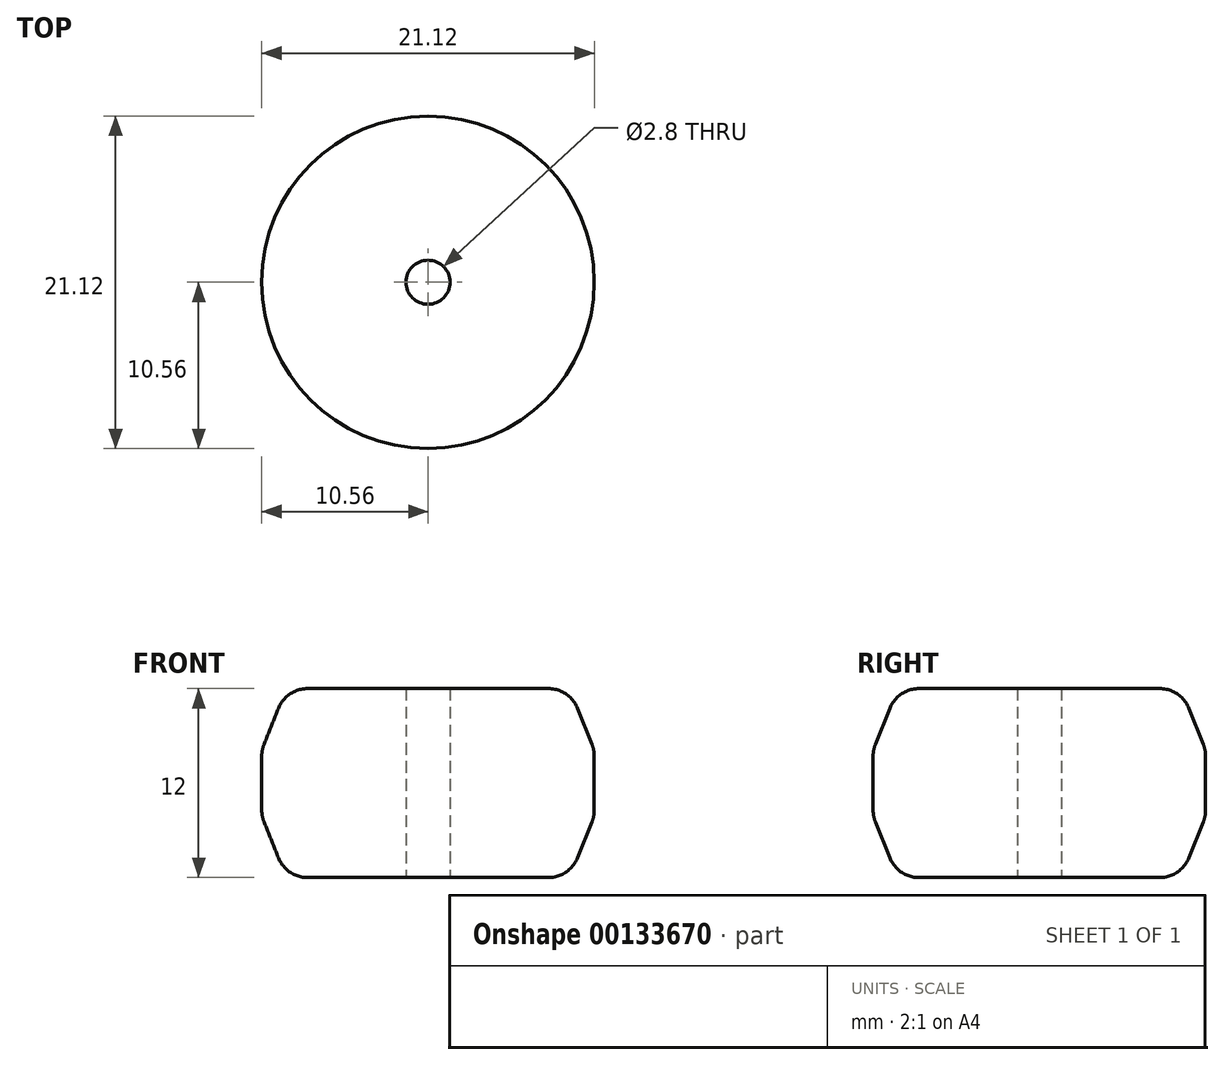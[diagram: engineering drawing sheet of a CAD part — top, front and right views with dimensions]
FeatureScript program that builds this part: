
annotation { "Feature Type Name" : "Feature", "Feature Type Description" : "" }
export const myFeature = defineFeature(function(context is Context, id is Id, definition is map)
    precondition{}
    {
        {
            var Q0;
            Q0=qCreatedBy(makeId("Top.planeOp"),FACE);
            var sketch = newSketch(context, id + "F0", { "sketchPlane" : qUnion([Q0])});
            skCircle(sketch, "E0", {"center": v(0, 0) * mm, "radius": 1.4 * mm});
            skCircle(sketch, "E1", {"center": v(0, 0) * mm, "radius": 9 * mm});
            skSolve(sketch);
        }
        {
            var Q0;
            Q0=makeQuery(id+"F0.imprint","IMPRINT",FACE,{"disambiguationData":[TD([[makeQuery(id+"F0.imprint","IMPRINT",EDGE,{"derivedFrom":sQuery(id+"F0.wireOp",EDGE,"E0")}),-1.0]])]});
            extrude(context, id + "F1", {"entities" : qUnion([Q0]), "depth" : 12 * mm});
        }
        {
            var Q0;
            Q0=qCreatedBy(makeId("Front.planeOp"),FACE);
            var sketch = newSketch(context, id + "F2", { "sketchPlane" : qUnion([Q0])});
            skLineSegment(sketch, "E2", {"start": v(-9, 0) * mm, "end": v(-9, 12) * mm});
            skLineSegment(sketch, "E3", {"start": v(-9, 0) * mm, "end": v(0, 0) * mm});
            skLineSegment(sketch, "E4", {"start": v(-9, 0) * mm, "end": v(-10.56, 3.9) * mm});
            skLineSegment(sketch, "E5", {"start": v(-10.56, 3.9) * mm, "end": v(-10.56, 8.1) * mm});
            skLineSegment(sketch, "E6", {"start": v(-10.56, 8.1) * mm, "end": v(-9, 12) * mm});
            skSolve(sketch);
        }
        {
            var Q0;
            Q0=qSketchRegion(id+"F2",true);
            var Q1;
            Q1=makeQuery(id+"F1.opExtrude","CAP_EDGE",EDGE,{"disambiguationData":[OSD([sQuery(id+"F0.wireOp",EDGE,"E1")])],"isStart":false});
            revolve(context, id + "F3", {"operationType" : NewBodyOperationType.ADD, "entities" : qUnion([Q0]), "axis" : qUnion([Q1]), "revolveType" : RevolveType.FULL, "oppositeDirection" : true});
        }
        {
            var Q0;
            Q0=makeQuery(id+"F3.opRevolve","SWEPT_EDGE",EDGE,{"disambiguationData":[OSD([sQuery(id+"F2.wireOp",EDGE,"E4"),sQuery(id+"F2.wireOp",EDGE,"E5")])]});
            var Q1;
            Q1=makeQuery(id+"F3.opRevolve","SWEPT_EDGE",EDGE,{"disambiguationData":[OSD([sQuery(id+"F2.wireOp",EDGE,"E5"),sQuery(id+"F2.wireOp",EDGE,"E6")])]});
            var Q2;
            Q2=makeQuery(id+"F3.boolean.opBoolean","MERGE",EDGE,{"derivedFrom":[makeQuery(id+"F1.opExtrude","CAP_EDGE",EDGE,{"disambiguationData":[OSD([sQuery(id+"F0.wireOp",EDGE,"E1")])],"isStart":true}),makeQuery(id+"F3.opRevolve","SWEPT_EDGE",EDGE,{"disambiguationData":[OSD([sQuery(id+"F2.wireOp",EDGE,"E2"),sQuery(id+"F2.wireOp",EDGE,"E4")])]})]});
            var Q3;
            Q3=makeQuery(id+"F3.boolean.opBoolean","MERGE",EDGE,{"derivedFrom":[makeQuery(id+"F1.opExtrude","CAP_EDGE",EDGE,{"disambiguationData":[OSD([sQuery(id+"F0.wireOp",EDGE,"E1")])],"isStart":false}),makeQuery(id+"F3.opRevolve","SWEPT_EDGE",EDGE,{"disambiguationData":[OSD([sQuery(id+"F2.wireOp",EDGE,"E2"),sQuery(id+"F2.wireOp",EDGE,"E6")])]})]});
            fillet(context, id + "F4", {"entities" : qUnion([Q0, Q1, Q2, Q3]), "radius" : 2 * mm, "tangentPropagation" : true, "allowEdgeOverflow" : false});
        }
    });
